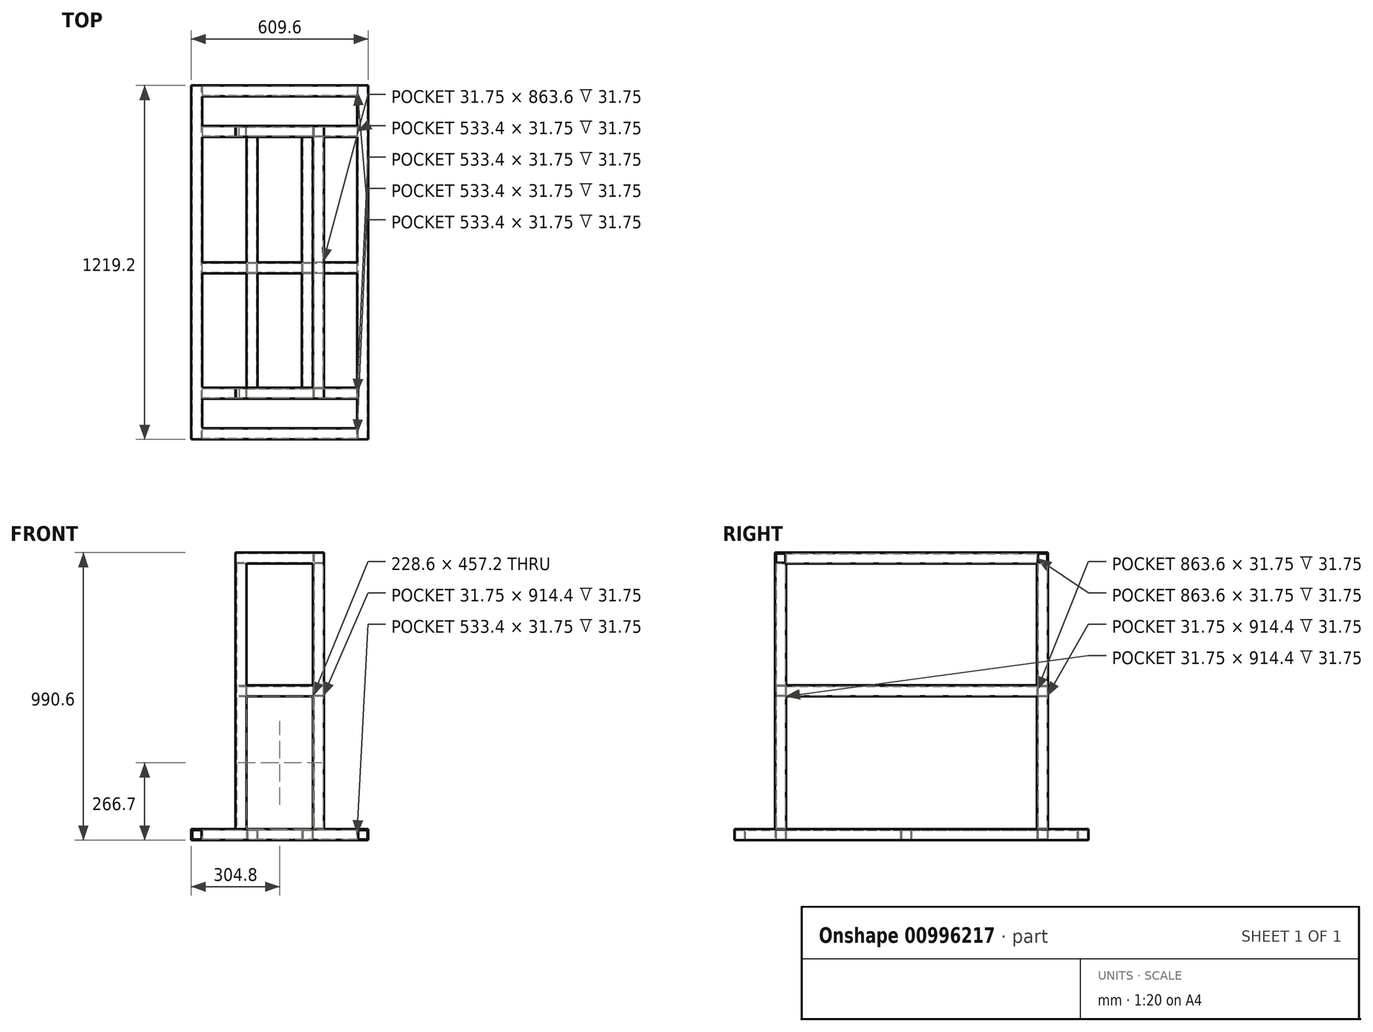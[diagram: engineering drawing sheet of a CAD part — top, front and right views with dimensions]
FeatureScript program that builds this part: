
annotation { "Feature Type Name" : "Feature", "Feature Type Description" : "" }
export const myFeature = defineFeature(function(context is Context, id is Id, definition is map)
    precondition{}
    {
        {
            var Q0;
            Q0=qCreatedBy(makeId("Front.planeOp"),FACE);
            var sketch = newSketch(context, id + "F0", { "sketchPlane" : qUnion([Q0])});
            skLineSegment(sketch, "E0.bottom", {"start": v(0, 0) * mm, "end": v(38.1, 0) * mm});
            skLineSegment(sketch, "E0.top", {"start": v(0, 38.1) * mm, "end": v(38.1, 38.1) * mm});
            skLineSegment(sketch, "E0.left", {"start": v(0, 0) * mm, "end": v(0, 38.1) * mm});
            skLineSegment(sketch, "E0.right", {"start": v(38.1, 0) * mm, "end": v(38.1, 38.1) * mm});
            skLineSegment(sketch, "E1.0", {"start": v(3.17, 3.18) * mm, "end": v(3.17, 34.93) * mm});
            skLineSegment(sketch, "E1.1", {"start": v(3.18, 3.18) * mm, "end": v(34.92, 3.18) * mm});
            skLineSegment(sketch, "E1.2", {"start": v(34.92, 3.18) * mm, "end": v(34.92, 34.93) * mm});
            skLineSegment(sketch, "E1.3", {"start": v(3.17, 34.93) * mm, "end": v(34.92, 34.93) * mm});
            skSolve(sketch);
        }
        {
            var Q0;
            Q0 = qSketchRegion(id + "F0", true);
            extrude(context, id + "F1", {"entities" : qUnion([Q0]), "depth" : 1219.2 * mm, "offsetDistance" : 25.4 * mm});
        }
        {
            var Q0;
            Q0=makeQuery(id+"F1.opExtrude","SWEPT_FACE",FACE,{"disambiguationData":[OSD([sQuery(id+"F0.wireOp",EDGE,"E0.right")])]});
            var sketch = newSketch(context, id + "F2", { "sketchPlane" : qUnion([Q0])});
            skLineSegment(sketch, "E2.bottom", {"start": v(-1219.2, 0) * mm, "end": v(-1181.1, 0) * mm});
            skLineSegment(sketch, "E2.top", {"start": v(-1219.2, 38.1) * mm, "end": v(-1181.1, 38.1) * mm});
            skLineSegment(sketch, "E2.left", {"start": v(-1219.2, 0) * mm, "end": v(-1219.2, 38.1) * mm});
            skLineSegment(sketch, "E2.right", {"start": v(-1181.1, 0) * mm, "end": v(-1181.1, 38.1) * mm});
            skLineSegment(sketch, "E3.bottom", {"start": v(0, 0) * mm, "end": v(-38.1, 0) * mm});
            skLineSegment(sketch, "E3.top", {"start": v(0, 38.1) * mm, "end": v(-38.1, 38.1) * mm});
            skLineSegment(sketch, "E3.left", {"start": v(0, 0) * mm, "end": v(0, 38.1) * mm});
            skLineSegment(sketch, "E3.right", {"start": v(-38.1, 0) * mm, "end": v(-38.1, 38.1) * mm});
            skLineSegment(sketch, "E4.0", {"start": v(-3.18, 3.18) * mm, "end": v(-34.93, 3.17) * mm});
            skLineSegment(sketch, "E4.1", {"start": v(-3.18, 3.18) * mm, "end": v(-3.18, 34.93) * mm});
            skLineSegment(sketch, "E4.2", {"start": v(-3.18, 34.93) * mm, "end": v(-34.93, 34.93) * mm});
            skLineSegment(sketch, "E4.3", {"start": v(-34.93, 3.17) * mm, "end": v(-34.93, 34.92) * mm});
            skLineSegment(sketch, "E5.0", {"start": v(-1216.03, 34.93) * mm, "end": v(-1184.27, 34.93) * mm});
            skLineSegment(sketch, "E5.1", {"start": v(-1216.03, 3.17) * mm, "end": v(-1216.03, 34.93) * mm});
            skLineSegment(sketch, "E5.2", {"start": v(-1216.03, 3.17) * mm, "end": v(-1184.27, 3.17) * mm});
            skLineSegment(sketch, "E5.3", {"start": v(-1184.27, 3.17) * mm, "end": v(-1184.27, 34.93) * mm});
            skSolve(sketch);
        }
        {
            var Q0;
            Q0 = qSketchRegion(id + "F2", true);
            extrude(context, id + "F3", {"entities" : qUnion([Q0]), "operationType" : NewBodyOperationType.ADD, "depth" : 533.4 * mm, "offsetDistance" : 25.4 * mm});
        }
        {
            var Q0;
            Q0=makeQuery(id+"F3.boolean.opBoolean","MERGE",FACE,{"derivedFrom":[makeQuery(id+"F1.opExtrude","CAP_FACE",FACE,{"disambiguationData":[OSD([sQuery(id+"F0.wireOp",EDGE,"E0.bottom"),sQuery(id+"F0.wireOp",EDGE,"E0.top"),sQuery(id+"F0.wireOp",EDGE,"E0.left"),sQuery(id+"F0.wireOp",EDGE,"E0.right"),sQuery(id+"F0.wireOp",EDGE,"E1.0"),sQuery(id+"F0.wireOp",EDGE,"E1.1"),sQuery(id+"F0.wireOp",EDGE,"E1.2"),sQuery(id+"F0.wireOp",EDGE,"E1.3")])],"isStart":true}),makeQuery(id+"F3.opExtrude","SWEPT_FACE",FACE,{"disambiguationData":[OSD([sQuery(id+"F2.wireOp",EDGE,"E3.left")])]})]});
            var sketch = newSketch(context, id + "F4", { "sketchPlane" : qUnion([Q0])});
            skLineSegment(sketch, "E6.bottom", {"start": v(-571.5, 38.1) * mm, "end": v(-609.6, 38.1) * mm});
            skLineSegment(sketch, "E6.top", {"start": v(-571.5, 0) * mm, "end": v(-609.6, 0) * mm});
            skLineSegment(sketch, "E6.left", {"start": v(-571.5, 38.1) * mm, "end": v(-571.5, 0) * mm});
            skLineSegment(sketch, "E6.right", {"start": v(-609.6, 38.1) * mm, "end": v(-609.6, 0) * mm});
            skLineSegment(sketch, "E7.0", {"start": v(-606.43, 34.92) * mm, "end": v(-606.43, 3.18) * mm});
            skLineSegment(sketch, "E7.1", {"start": v(-574.68, 34.92) * mm, "end": v(-606.43, 34.92) * mm});
            skLineSegment(sketch, "E7.2", {"start": v(-574.68, 34.92) * mm, "end": v(-574.68, 3.18) * mm});
            skLineSegment(sketch, "E7.3", {"start": v(-574.68, 3.18) * mm, "end": v(-606.43, 3.18) * mm});
            skSolve(sketch);
        }
        {
            var Q0;
            Q0 = qSketchRegion(id + "F4", true);
            extrude(context, id + "F5", {"entities" : qUnion([Q0]), "operationType" : NewBodyOperationType.ADD, "oppositeDirection" : true, "depth" : 1219.2 * mm, "offsetDistance" : 25.4 * mm});
        }
        {
            var Q0;
            Q0=makeQuery(id+"F3.boolean.opBoolean","SPLIT",FACE,{"disambiguationData":[TD([makeQuery(id+"F1.opExtrude","SWEPT_FACE",FACE,{"disambiguationData":[OSD([sQuery(id+"F0.wireOp",EDGE,"E0.bottom")])]})])],"derivedFrom":makeQuery(id+"F1.opExtrude","SWEPT_FACE",FACE,{"disambiguationData":[OSD([sQuery(id+"F0.wireOp",EDGE,"E0.right")])]})});
            var sketch = newSketch(context, id + "F6", { "sketchPlane" : qUnion([Q0])});
            skLineSegment(sketch, "E8.bottom", {"start": v(-1079.5, 38.1) * mm, "end": v(-1041.4, 38.1) * mm});
            skLineSegment(sketch, "E8.top", {"start": v(-1079.5, 0) * mm, "end": v(-1041.4, 0) * mm});
            skLineSegment(sketch, "E8.left", {"start": v(-1079.5, 38.1) * mm, "end": v(-1079.5, 0) * mm});
            skLineSegment(sketch, "E8.right", {"start": v(-1041.4, 38.1) * mm, "end": v(-1041.4, 0) * mm});
            skLineSegment(sketch, "E9.bottom", {"start": v(-139.7, 38.1) * mm, "end": v(-177.8, 38.1) * mm});
            skLineSegment(sketch, "E9.top", {"start": v(-139.7, 0) * mm, "end": v(-177.8, 0) * mm});
            skLineSegment(sketch, "E9.left", {"start": v(-139.7, 38.1) * mm, "end": v(-139.7, 0) * mm});
            skLineSegment(sketch, "E9.right", {"start": v(-177.8, 38.1) * mm, "end": v(-177.8, 0) * mm});
            skLineSegment(sketch, "E10.0", {"start": v(-1076.33, 34.93) * mm, "end": v(-1076.33, 3.17) * mm});
            skLineSegment(sketch, "E10.1", {"start": v(-1076.33, 34.92) * mm, "end": v(-1044.57, 34.92) * mm});
            skLineSegment(sketch, "E10.2", {"start": v(-1044.57, 34.93) * mm, "end": v(-1044.57, 3.17) * mm});
            skLineSegment(sketch, "E10.3", {"start": v(-1076.33, 3.18) * mm, "end": v(-1044.57, 3.18) * mm});
            skLineSegment(sketch, "E11.0", {"start": v(-142.88, 34.93) * mm, "end": v(-174.63, 34.93) * mm});
            skLineSegment(sketch, "E11.1", {"start": v(-142.88, 34.93) * mm, "end": v(-142.88, 3.18) * mm});
            skLineSegment(sketch, "E11.2", {"start": v(-142.88, 3.18) * mm, "end": v(-174.63, 3.18) * mm});
            skLineSegment(sketch, "E11.3", {"start": v(-174.63, 34.93) * mm, "end": v(-174.63, 3.18) * mm});
            skLineSegment(sketch, "E12.bottom", {"start": v(-647.7, 38.1) * mm, "end": v(-609.6, 38.1) * mm});
            skLineSegment(sketch, "E12.top", {"start": v(-647.7, 0) * mm, "end": v(-609.6, 0) * mm});
            skLineSegment(sketch, "E12.left", {"start": v(-647.7, 38.1) * mm, "end": v(-647.7, 0) * mm});
            skLineSegment(sketch, "E12.right", {"start": v(-609.6, 38.1) * mm, "end": v(-609.6, 0) * mm});
            skLineSegment(sketch, "E13.0", {"start": v(-644.52, 34.93) * mm, "end": v(-612.77, 34.93) * mm});
            skLineSegment(sketch, "E13.1", {"start": v(-644.52, 34.93) * mm, "end": v(-644.52, 3.17) * mm});
            skLineSegment(sketch, "E13.2", {"start": v(-644.52, 3.17) * mm, "end": v(-612.77, 3.17) * mm});
            skLineSegment(sketch, "E13.3", {"start": v(-612.77, 34.93) * mm, "end": v(-612.77, 3.17) * mm});
            skSolve(sketch);
        }
        {
            var Q0;
            Q0 = qSketchRegion(id + "F6", true);
            extrude(context, id + "F7", {"entities" : qUnion([Q0]), "operationType" : NewBodyOperationType.ADD, "depth" : 533.4 * mm, "offsetDistance" : 25.4 * mm});
        }
        {
            var Q0;
            Q0=makeQuery(id+"F7.opExtrude","SWEPT_FACE",FACE,{"disambiguationData":[OSD([sQuery(id+"F6.wireOp",EDGE,"E9.right")])]});
            var sketch = newSketch(context, id + "F8", { "sketchPlane" : qUnion([Q0])});
            skLineSegment(sketch, "E14.bottom", {"start": v(190.5, 38.1) * mm, "end": v(228.6, 38.1) * mm});
            skLineSegment(sketch, "E14.top", {"start": v(190.5, 0) * mm, "end": v(228.6, 0) * mm});
            skLineSegment(sketch, "E14.left", {"start": v(190.5, 38.1) * mm, "end": v(190.5, 0) * mm});
            skLineSegment(sketch, "E14.right", {"start": v(228.6, 38.1) * mm, "end": v(228.6, 0) * mm});
            skLineSegment(sketch, "E15.bottom", {"start": v(381, 38.1) * mm, "end": v(419.1, 38.1) * mm});
            skLineSegment(sketch, "E15.top", {"start": v(381, 0) * mm, "end": v(419.1, 0) * mm});
            skLineSegment(sketch, "E15.left", {"start": v(381, 38.1) * mm, "end": v(381, 0) * mm});
            skLineSegment(sketch, "E15.right", {"start": v(419.1, 38.1) * mm, "end": v(419.1, 0) * mm});
            skLineSegment(sketch, "E16.0", {"start": v(193.68, 34.93) * mm, "end": v(193.68, 3.18) * mm});
            skLineSegment(sketch, "E16.1", {"start": v(193.68, 34.93) * mm, "end": v(225.42, 34.93) * mm});
            skLineSegment(sketch, "E16.2", {"start": v(225.42, 34.93) * mm, "end": v(225.42, 3.18) * mm});
            skLineSegment(sketch, "E16.3", {"start": v(193.68, 3.18) * mm, "end": v(225.42, 3.18) * mm});
            skLineSegment(sketch, "E17.0", {"start": v(384.18, 34.93) * mm, "end": v(384.18, 3.18) * mm});
            skLineSegment(sketch, "E17.1", {"start": v(384.18, 34.93) * mm, "end": v(415.93, 34.93) * mm});
            skLineSegment(sketch, "E17.2", {"start": v(415.93, 34.93) * mm, "end": v(415.93, 3.18) * mm});
            skLineSegment(sketch, "E17.3", {"start": v(384.18, 3.18) * mm, "end": v(415.93, 3.18) * mm});
            skSolve(sketch);
        }
        {
            var Q0;
            Q0 = qSketchRegion(id + "F8", true);
            extrude(context, id + "F9", {"entities" : qUnion([Q0]), "operationType" : NewBodyOperationType.ADD, "depth" : 863.6 * mm, "offsetDistance" : 25.4 * mm});
        }
        {
            var Q0;
            Q0=makeQuery(id+"F9.boolean.opBoolean","MERGE",FACE,{"derivedFrom":[makeQuery(id+"F7.boolean.opBoolean","MERGE",FACE,{"derivedFrom":[makeQuery(id+"F5.boolean.opBoolean","MERGE",FACE,{"derivedFrom":[makeQuery(id+"F3.boolean.opBoolean","MERGE",FACE,{"derivedFrom":[makeQuery(id+"F1.opExtrude","SWEPT_FACE",FACE,{"disambiguationData":[OSD([sQuery(id+"F0.wireOp",EDGE,"E0.top")])]}),makeQuery(id+"F3.opExtrude","SWEPT_FACE",FACE,{"disambiguationData":[OSD([sQuery(id+"F2.wireOp",EDGE,"E2.top")])]}),makeQuery(id+"F3.opExtrude","SWEPT_FACE",FACE,{"disambiguationData":[OSD([sQuery(id+"F2.wireOp",EDGE,"E3.top")])]})]}),makeQuery(id+"F5.opExtrude","SWEPT_FACE",FACE,{"disambiguationData":[OSD([sQuery(id+"F4.wireOp",EDGE,"E6.bottom")])]})]}),makeQuery(id+"F7.opExtrude","SWEPT_FACE",FACE,{"disambiguationData":[OSD([sQuery(id+"F6.wireOp",EDGE,"E8.bottom")])]}),makeQuery(id+"F7.opExtrude","SWEPT_FACE",FACE,{"disambiguationData":[OSD([sQuery(id+"F6.wireOp",EDGE,"E9.bottom")])]}),makeQuery(id+"F7.opExtrude","SWEPT_FACE",FACE,{"disambiguationData":[OSD([sQuery(id+"F6.wireOp",EDGE,"E12.bottom")])]})]}),makeQuery(id+"F9.opExtrude","SWEPT_FACE",FACE,{"disambiguationData":[OSD([sQuery(id+"F8.wireOp",EDGE,"E14.bottom")])]}),makeQuery(id+"F9.opExtrude","SWEPT_FACE",FACE,{"disambiguationData":[OSD([sQuery(id+"F8.wireOp",EDGE,"E15.bottom")])]})]});
            var sketch = newSketch(context, id + "F10", { "sketchPlane" : qUnion([Q0])});
            skLineSegment(sketch, "E18.bottom", {"start": v(457.2, -139.7) * mm, "end": v(419.1, -139.7) * mm});
            skLineSegment(sketch, "E18.top", {"start": v(457.2, -177.8) * mm, "end": v(419.1, -177.8) * mm});
            skLineSegment(sketch, "E18.left", {"start": v(457.2, -139.7) * mm, "end": v(457.2, -177.8) * mm});
            skLineSegment(sketch, "E18.right", {"start": v(419.1, -139.7) * mm, "end": v(419.1, -177.8) * mm});
            skLineSegment(sketch, "E19.bottom", {"start": v(190.5, -139.7) * mm, "end": v(152.4, -139.7) * mm});
            skLineSegment(sketch, "E19.top", {"start": v(190.5, -177.8) * mm, "end": v(152.4, -177.8) * mm});
            skLineSegment(sketch, "E19.left", {"start": v(190.5, -139.7) * mm, "end": v(190.5, -177.8) * mm});
            skLineSegment(sketch, "E19.right", {"start": v(152.4, -139.7) * mm, "end": v(152.4, -177.8) * mm});
            skLineSegment(sketch, "E20.bottom", {"start": v(457.2, -1041.4) * mm, "end": v(419.1, -1041.4) * mm});
            skLineSegment(sketch, "E20.top", {"start": v(457.2, -1079.5) * mm, "end": v(419.1, -1079.5) * mm});
            skLineSegment(sketch, "E20.left", {"start": v(457.2, -1041.4) * mm, "end": v(457.2, -1079.5) * mm});
            skLineSegment(sketch, "E20.right", {"start": v(419.1, -1041.4) * mm, "end": v(419.1, -1079.5) * mm});
            skLineSegment(sketch, "E21.bottom", {"start": v(190.5, -1041.4) * mm, "end": v(152.4, -1041.4) * mm});
            skLineSegment(sketch, "E21.top", {"start": v(190.5, -1079.5) * mm, "end": v(152.4, -1079.5) * mm});
            skLineSegment(sketch, "E21.left", {"start": v(190.5, -1041.4) * mm, "end": v(190.5, -1079.5) * mm});
            skLineSegment(sketch, "E21.right", {"start": v(152.4, -1041.4) * mm, "end": v(152.4, -1079.5) * mm});
            skLineSegment(sketch, "E22.0", {"start": v(454.03, -142.88) * mm, "end": v(454.03, -174.63) * mm});
            skLineSegment(sketch, "E22.1", {"start": v(454.03, -142.88) * mm, "end": v(422.28, -142.88) * mm});
            skLineSegment(sketch, "E22.2", {"start": v(422.28, -142.88) * mm, "end": v(422.28, -174.63) * mm});
            skLineSegment(sketch, "E22.3", {"start": v(454.03, -174.63) * mm, "end": v(422.28, -174.63) * mm});
            skLineSegment(sketch, "E23.0", {"start": v(187.32, -142.88) * mm, "end": v(187.32, -174.63) * mm});
            skLineSegment(sketch, "E23.1", {"start": v(187.32, -142.88) * mm, "end": v(155.58, -142.88) * mm});
            skLineSegment(sketch, "E23.2", {"start": v(155.58, -142.88) * mm, "end": v(155.58, -174.63) * mm});
            skLineSegment(sketch, "E23.3", {"start": v(187.32, -174.63) * mm, "end": v(155.58, -174.63) * mm});
            skLineSegment(sketch, "E24.0", {"start": v(187.33, -1044.57) * mm, "end": v(187.33, -1076.33) * mm});
            skLineSegment(sketch, "E24.1", {"start": v(187.33, -1044.57) * mm, "end": v(155.58, -1044.57) * mm});
            skLineSegment(sketch, "E24.2", {"start": v(155.58, -1044.57) * mm, "end": v(155.58, -1076.33) * mm});
            skLineSegment(sketch, "E24.3", {"start": v(187.33, -1076.33) * mm, "end": v(155.58, -1076.33) * mm});
            skLineSegment(sketch, "E25.0", {"start": v(454.03, -1044.57) * mm, "end": v(454.03, -1076.33) * mm});
            skLineSegment(sketch, "E25.1", {"start": v(454.03, -1044.57) * mm, "end": v(422.28, -1044.57) * mm});
            skLineSegment(sketch, "E25.2", {"start": v(422.28, -1044.57) * mm, "end": v(422.28, -1076.33) * mm});
            skLineSegment(sketch, "E25.3", {"start": v(454.03, -1076.33) * mm, "end": v(422.28, -1076.33) * mm});
            skSolve(sketch);
        }
        {
            var Q0;
            Q0 = qSketchRegion(id + "F10", true);
            extrude(context, id + "F11", {"entities" : qUnion([Q0]), "operationType" : NewBodyOperationType.ADD, "depth" : 914.4 * mm, "offsetDistance" : 25.4 * mm});
        }
        {
            var Q0;
            Q0=makeQuery(id+"F11.opExtrude","SWEPT_FACE",FACE,{"disambiguationData":[OSD([sQuery(id+"F10.wireOp",EDGE,"E21.right")])]});
            var sketch = newSketch(context, id + "F12", { "sketchPlane" : qUnion([Q0])});
            skLineSegment(sketch, "E26.bottom", {"start": v(1079.5, 952.5) * mm, "end": v(1041.4, 952.5) * mm});
            skLineSegment(sketch, "E26.top", {"start": v(1079.5, 990.6) * mm, "end": v(1041.4, 990.6) * mm});
            skLineSegment(sketch, "E26.left", {"start": v(1079.5, 952.5) * mm, "end": v(1079.5, 990.6) * mm});
            skLineSegment(sketch, "E26.right", {"start": v(1041.4, 952.5) * mm, "end": v(1041.4, 990.6) * mm});
            skLineSegment(sketch, "E27.bottom", {"start": v(177.8, 952.5) * mm, "end": v(139.7, 952.5) * mm});
            skLineSegment(sketch, "E27.top", {"start": v(177.8, 990.6) * mm, "end": v(139.7, 990.6) * mm});
            skLineSegment(sketch, "E27.left", {"start": v(177.8, 952.5) * mm, "end": v(177.8, 990.6) * mm});
            skLineSegment(sketch, "E27.right", {"start": v(139.7, 952.5) * mm, "end": v(139.7, 990.6) * mm});
            skLineSegment(sketch, "E28.0", {"start": v(1076.33, 955.68) * mm, "end": v(1076.33, 987.43) * mm});
            skLineSegment(sketch, "E28.1", {"start": v(1076.33, 955.68) * mm, "end": v(1044.57, 955.68) * mm});
            skLineSegment(sketch, "E28.2", {"start": v(1044.57, 955.68) * mm, "end": v(1044.57, 987.43) * mm});
            skLineSegment(sketch, "E28.3", {"start": v(1076.33, 987.43) * mm, "end": v(1044.57, 987.43) * mm});
            skLineSegment(sketch, "E29.0", {"start": v(174.63, 987.42) * mm, "end": v(142.88, 987.42) * mm});
            skLineSegment(sketch, "E29.1", {"start": v(174.63, 955.68) * mm, "end": v(174.63, 987.42) * mm});
            skLineSegment(sketch, "E29.2", {"start": v(174.63, 955.68) * mm, "end": v(142.88, 955.68) * mm});
            skLineSegment(sketch, "E29.3", {"start": v(142.88, 955.68) * mm, "end": v(142.88, 987.42) * mm});
            skSolve(sketch);
        }
        {
            var Q0;
            Q0 = qSketchRegion(id + "F12", true);
            extrude(context, id + "F13", {"entities" : qUnion([Q0]), "operationType" : NewBodyOperationType.ADD, "oppositeDirection" : true, "depth" : 304.8 * mm, "offsetDistance" : 25.4 * mm});
        }
        {
            var Q0;
            {var subQ18=makeQuery(id+"F7.opExtrude","SWEPT_FACE",FACE,{"disambiguationData":[OSD([sQuery(id+"F6.wireOp",EDGE,"E9.right")])]});Q0=makeQuery(id+"F13.boolean.opBoolean","MERGE",FACE,{"derivedFrom":[makeQuery(id+"F11.boolean.opBoolean","MERGE",FACE,{"derivedFrom":[makeQuery(id+"F9.boolean.opBoolean","SPLIT",FACE,{"disambiguationData":[TD([makeQuery(id+"F1.opExtrude","SWEPT_FACE",FACE,{"disambiguationData":[OSD([sQuery(id+"F0.wireOp",EDGE,"E0.right")])]})])],"derivedFrom":subQ18}),makeQuery(id+"F11.opExtrude","SWEPT_FACE",FACE,{"disambiguationData":[OSD([sQuery(id+"F10.wireOp",EDGE,"E19.top")])]})]}),makeQuery(id+"F11.boolean.opBoolean","MERGE",FACE,{"derivedFrom":[makeQuery(id+"F9.boolean.opBoolean","SPLIT",FACE,{"disambiguationData":[TD([makeQuery(id+"F5.opExtrude","SWEPT_FACE",FACE,{"disambiguationData":[OSD([sQuery(id+"F4.wireOp",EDGE,"E6.left")])]})])],"derivedFrom":subQ18}),makeQuery(id+"F11.opExtrude","SWEPT_FACE",FACE,{"disambiguationData":[OSD([sQuery(id+"F10.wireOp",EDGE,"E18.top")])]})]}),makeQuery(id+"F13.opExtrude","SWEPT_FACE",FACE,{"disambiguationData":[OSD([sQuery(id+"F12.wireOp",EDGE,"E27.left")])]})]});}
            var sketch = newSketch(context, id + "F14", { "sketchPlane" : qUnion([Q0])});
            skLineSegment(sketch, "E30.bottom", {"start": v(457.2, 990.6) * mm, "end": v(419.1, 990.6) * mm});
            skLineSegment(sketch, "E30.top", {"start": v(457.2, 952.5) * mm, "end": v(419.1, 952.5) * mm});
            skLineSegment(sketch, "E30.left", {"start": v(457.2, 990.6) * mm, "end": v(457.2, 952.5) * mm});
            skLineSegment(sketch, "E30.right", {"start": v(419.1, 990.6) * mm, "end": v(419.1, 952.5) * mm});
            skLineSegment(sketch, "E31.0", {"start": v(454.03, 987.42) * mm, "end": v(422.28, 987.42) * mm});
            skLineSegment(sketch, "E31.1", {"start": v(454.02, 987.42) * mm, "end": v(454.02, 955.68) * mm});
            skLineSegment(sketch, "E31.2", {"start": v(454.03, 955.68) * mm, "end": v(422.28, 955.68) * mm});
            skLineSegment(sketch, "E31.3", {"start": v(422.28, 987.42) * mm, "end": v(422.28, 955.68) * mm});
            skLineSegment(sketch, "E32.0.1.0", {"start": v(454.03, 498.48) * mm, "end": v(422.28, 498.48) * mm});
            skLineSegment(sketch, "E32.0.1.1", {"start": v(422.28, 530.22) * mm, "end": v(422.28, 498.48) * mm});
            skLineSegment(sketch, "E32.0.1.2", {"start": v(457.2, 533.4) * mm, "end": v(457.2, 495.3) * mm});
            skLineSegment(sketch, "E32.0.1.3", {"start": v(419.1, 533.4) * mm, "end": v(419.1, 495.3) * mm});
            skLineSegment(sketch, "E32.0.1.4", {"start": v(454.03, 530.22) * mm, "end": v(454.03, 498.48) * mm});
            skLineSegment(sketch, "E32.0.1.5", {"start": v(457.2, 495.3) * mm, "end": v(419.1, 495.3) * mm});
            skLineSegment(sketch, "E32.0.1.6", {"start": v(457.2, 533.4) * mm, "end": v(419.1, 533.4) * mm});
            skLineSegment(sketch, "E32.0.1.7", {"start": v(454.03, 530.22) * mm, "end": v(422.28, 530.22) * mm});
            skLineSegment(sketch, "E32.direction1", {"start": v(419.1, 952.5) * mm, "end": v(419.35, 952.5) * mm, "construction": true});
            skLineSegment(sketch, "E32.direction2", {"start": v(419.1, 952.5) * mm, "end": v(419.1, 495.3) * mm, "construction": true});
            skSolve(sketch);
        }
        {
            var Q0;
            Q0 = qSketchRegion(id + "F14", true);
            extrude(context, id + "F15", {"entities" : qUnion([Q0]), "operationType" : NewBodyOperationType.ADD, "depth" : 863.6 * mm, "offsetDistance" : 25.4 * mm});
        }
        {
            var Q0;
            Q0=makeQuery(id+"F15.boolean.opBoolean","MERGE",FACE,{"derivedFrom":[makeQuery(id+"F11.opExtrude","SWEPT_FACE",FACE,{"disambiguationData":[OSD([sQuery(id+"F10.wireOp",EDGE,"E18.right")])]}),makeQuery(id+"F11.opExtrude","SWEPT_FACE",FACE,{"disambiguationData":[OSD([sQuery(id+"F10.wireOp",EDGE,"E20.right")])]}),makeQuery(id+"F15.opExtrude","SWEPT_FACE",FACE,{"disambiguationData":[OSD([sQuery(id+"F14.wireOp",EDGE,"E32.0.1.3")])]})]});
            var sketch = newSketch(context, id + "F16", { "sketchPlane" : qUnion([Q0])});
            skLineSegment(sketch, "E33.bottom", {"start": v(177.8, 533.4) * mm, "end": v(139.7, 533.4) * mm});
            skLineSegment(sketch, "E33.top", {"start": v(177.8, 495.3) * mm, "end": v(139.7, 495.3) * mm});
            skLineSegment(sketch, "E33.left", {"start": v(177.8, 533.4) * mm, "end": v(177.8, 495.3) * mm});
            skLineSegment(sketch, "E33.right", {"start": v(139.7, 533.4) * mm, "end": v(139.7, 495.3) * mm});
            skLineSegment(sketch, "E34.bottom", {"start": v(1041.4, 533.4) * mm, "end": v(1079.5, 533.4) * mm});
            skLineSegment(sketch, "E34.top", {"start": v(1041.4, 495.3) * mm, "end": v(1079.5, 495.3) * mm});
            skLineSegment(sketch, "E34.left", {"start": v(1041.4, 533.4) * mm, "end": v(1041.4, 495.3) * mm});
            skLineSegment(sketch, "E34.right", {"start": v(1079.5, 533.4) * mm, "end": v(1079.5, 495.3) * mm});
            skLineSegment(sketch, "E35.0", {"start": v(174.63, 530.22) * mm, "end": v(142.88, 530.22) * mm});
            skLineSegment(sketch, "E35.1", {"start": v(174.63, 530.22) * mm, "end": v(174.63, 498.48) * mm});
            skLineSegment(sketch, "E35.2", {"start": v(174.63, 498.48) * mm, "end": v(142.88, 498.48) * mm});
            skLineSegment(sketch, "E35.3", {"start": v(142.88, 530.22) * mm, "end": v(142.88, 498.48) * mm});
            skLineSegment(sketch, "E36.0", {"start": v(1044.58, 530.22) * mm, "end": v(1076.32, 530.22) * mm});
            skLineSegment(sketch, "E36.1", {"start": v(1044.58, 530.22) * mm, "end": v(1044.58, 498.48) * mm});
            skLineSegment(sketch, "E36.2", {"start": v(1044.58, 498.48) * mm, "end": v(1076.32, 498.48) * mm});
            skLineSegment(sketch, "E36.3", {"start": v(1076.32, 530.22) * mm, "end": v(1076.32, 498.48) * mm});
            skSolve(sketch);
        }
        {
            var Q0;
            Q0 = qSketchRegion(id + "F16", true);
            extrude(context, id + "F17", {"entities" : qUnion([Q0]), "operationType" : NewBodyOperationType.ADD, "depth" : 254 * mm, "offsetDistance" : 25.4 * mm});
        }
    });
